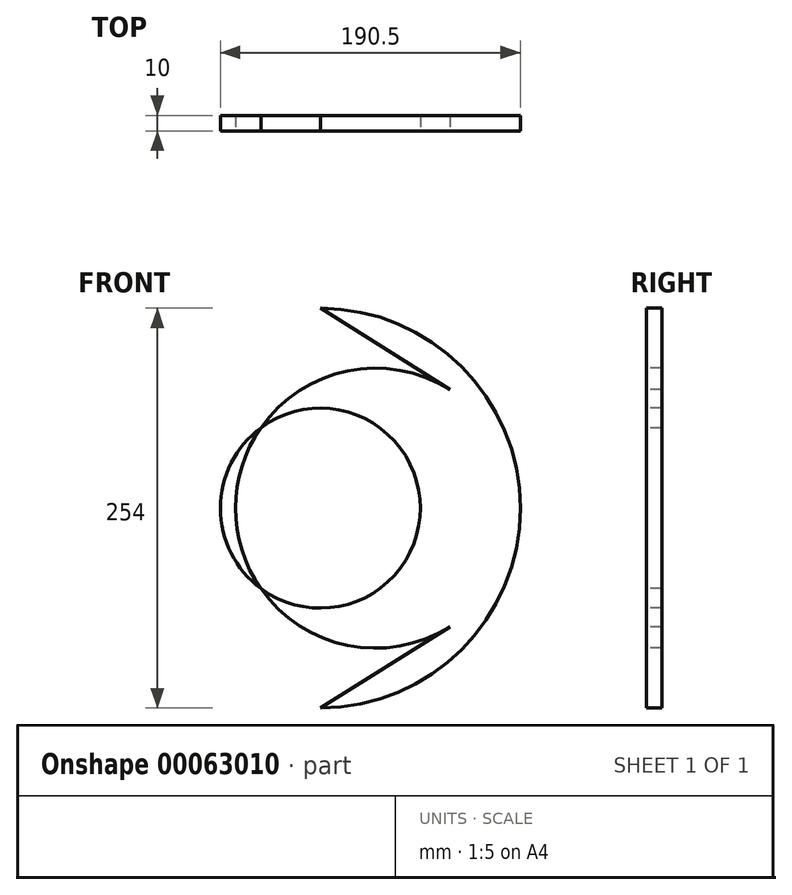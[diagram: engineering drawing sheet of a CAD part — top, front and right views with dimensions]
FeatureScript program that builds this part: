
annotation { "Feature Type Name" : "Feature", "Feature Type Description" : "" }
export const myFeature = defineFeature(function(context is Context, id is Id, definition is map)
    precondition{}
    {
        {
            var Q0;
            Q0=qCreatedBy(makeId("Front.planeOp"),FACE);
            var sketch = newSketch(context, id + "F0", { "sketchPlane" : qUnion([Q0])});
            skCircle(sketch, "E0", {"center": v(0, 0) * mm, "radius": 127 * mm});
            skCircle(sketch, "E1", {"center": v(35, 0) * mm, "radius": 88.9 * mm});
            skLineSegment(sketch, "E2", {"start": v(0, 127) * mm, "end": v(82.3, 75.27) * mm});
            skLineSegment(sketch, "E3", {"start": v(0, -127) * mm, "end": v(82.3, -75.27) * mm});
            skCircle(sketch, "E4", {"center": v(0, 0) * mm, "radius": 63.5 * mm});
            skCircle(sketch, "E5", {"center": v(35, 0) * mm, "radius": 1.5 * mm});
            skSolve(sketch);
        }
        {
            var Q0;
            {var subQ0=sQuery(id+"F0.wireOp",EDGE,"E2");var subQ1=sQuery(id+"F0.wireOp",EDGE,"E0");var subQ2=makeQuery(id+"F0.imprint","INTERSECT",VERTEX,{"disambiguationData":[OD(0.0)],"derivedFrom":[subQ1,subQ0]});Q0=makeQuery(id+"F0.imprint","IMPRINT",FACE,{"disambiguationData":[TD([[makeQuery(id+"F0.imprint","IMPRINT",EDGE,{"disambiguationData":[TD([[subQ2,1.0]])],"derivedFrom":subQ1}),1.0]])]});}
            var Q1;
            {var subQ0=sQuery(id+"F0.wireOp",EDGE,"E3");var subQ1=sQuery(id+"F0.wireOp",EDGE,"E0");var subQ2=makeQuery(id+"F0.imprint","INTERSECT",VERTEX,{"disambiguationData":[OD(0.0)],"derivedFrom":[subQ1,subQ0]});Q1=makeQuery(id+"F0.imprint","IMPRINT",FACE,{"disambiguationData":[TD([[makeQuery(id+"F0.imprint","IMPRINT",EDGE,{"disambiguationData":[TD([[subQ2,-1.0]])],"derivedFrom":subQ1}),1.0]])]});}
            var Q2;
            Q2=makeQuery(id+"F0.imprint","IMPRINT",FACE,{"disambiguationData":[TD([[makeQuery(id+"F0.imprint","IMPRINT",EDGE,{"derivedFrom":sQuery(id+"F0.wireOp",EDGE,"E4")}),-1.0]])]});
            var Q3;
            Q3=makeQuery(id+"F0.imprint","IMPRINT",FACE,{"disambiguationData":[TD([[makeQuery(id+"F0.imprint","IMPRINT",EDGE,{"derivedFrom":sQuery(id+"F0.wireOp",EDGE,"E4")}),1.0]])]});
            extrude(context, id + "F1", {"entities" : qUnion([Q0, Q1, Q2, Q3]), "oppositeDirection" : true, "depth" : 10 * mm});
        }
    });
